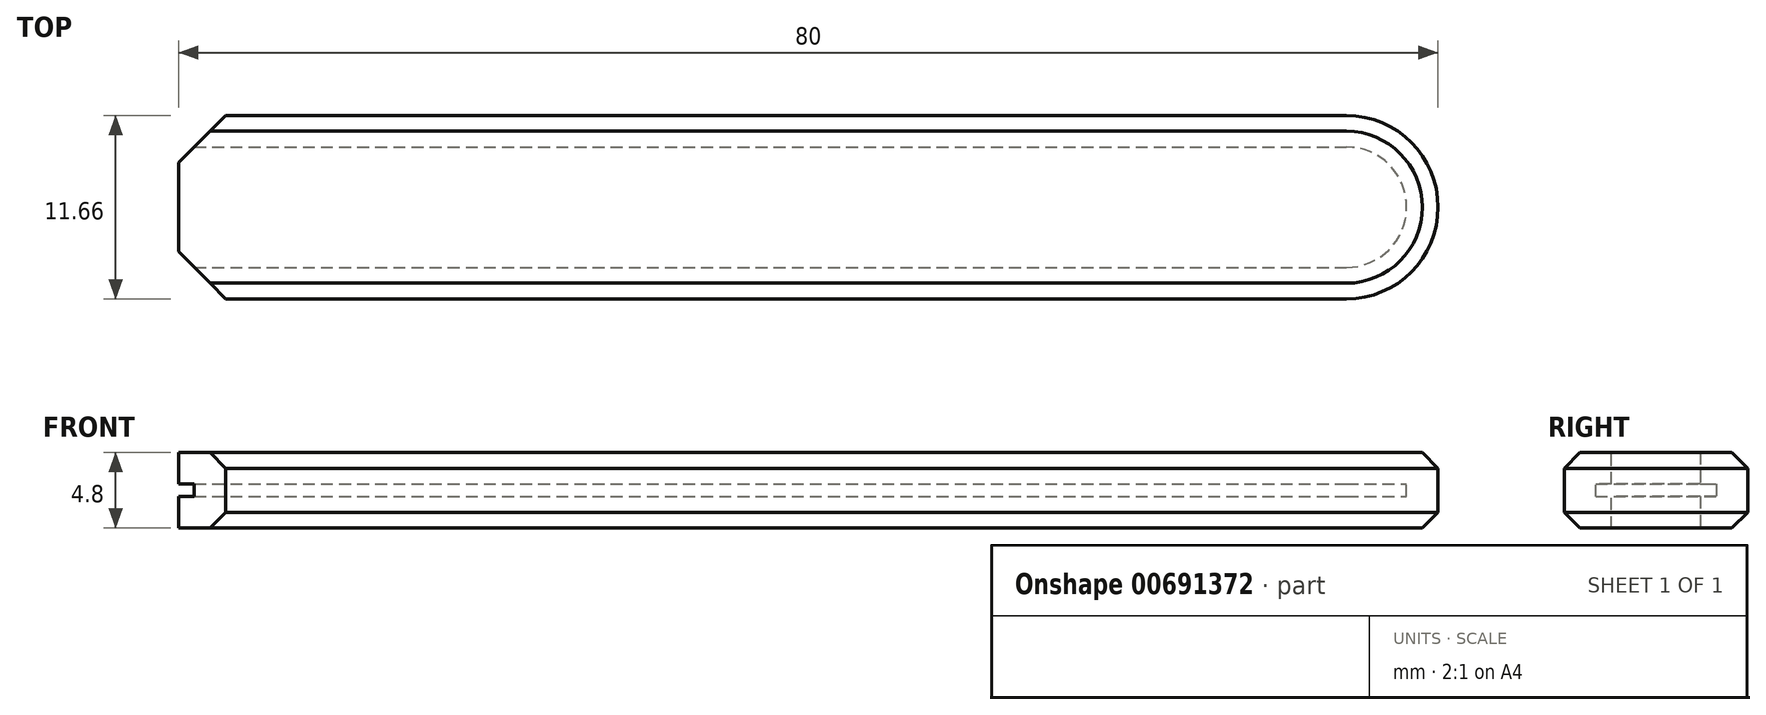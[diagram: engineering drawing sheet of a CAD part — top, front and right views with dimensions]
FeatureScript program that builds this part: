
annotation { "Feature Type Name" : "Feature", "Feature Type Description" : "" }
export const myFeature = defineFeature(function(context is Context, id is Id, definition is map)
    precondition{}
    {
        {
            var Q0;
            Q0=qCreatedBy(makeId("Top.planeOp"),FACE);
            var sketch = newSketch(context, id + "F0", { "sketchPlane" : qUnion([Q0])});
            skLineSegment(sketch, "E0.bottom", {"start": v(-39, -3.83) * mm, "end": v(35.17, -3.83) * mm});
            skLineSegment(sketch, "E0.top", {"start": v(-39, 3.82) * mm, "end": v(35.17, 3.82) * mm});
            skLineSegment(sketch, "E0.left", {"start": v(-39, -3.83) * mm, "end": v(-39, 3.82) * mm});
            skLineSegment(sketch, "E0.right", {"start": v(39, 0) * mm, "end": v(39, 0) * mm});
            skPoint(sketch, "E0.middle", {"position": v(0, 0) * mm});
            skPoint(sketch, "E1.visualSharp", {"position": v(39, 3.82) * mm});
            skArc(sketch, "E1.filletArc", {"start": v(39, 0) * mm, "mid": v(37.88, 2.7) * mm, "end": v(35.17, 3.82) * mm});
            skPoint(sketch, "E2.visualSharp", {"position": v(39, -3.83) * mm});
            skArc(sketch, "E2.filletArc", {"start": v(35.17, -3.83) * mm, "mid": v(37.88, -2.7) * mm, "end": v(39, 0) * mm});
            skLineSegment(sketch, "E3.0", {"start": v(-39, -5.83) * mm, "end": v(35.17, -5.83) * mm});
            skArc(sketch, "E3.1", {"start": v(35.17, -5.82) * mm, "mid": v(39.3, -4.12) * mm, "end": v(41, 0) * mm});
            skArc(sketch, "E3.2", {"start": v(41, 0) * mm, "mid": v(39.3, 4.12) * mm, "end": v(35.17, 5.82) * mm});
            skLineSegment(sketch, "E3.3", {"start": v(-39, 5.82) * mm, "end": v(35.17, 5.82) * mm});
            skLineSegment(sketch, "E4", {"start": v(-39, 5.82) * mm, "end": v(-39, 3.82) * mm});
            skLineSegment(sketch, "E5", {"start": v(-39, -5.83) * mm, "end": v(-39, -3.83) * mm});
            skSolve(sketch);
        }
        {
            var Q0;
            Q0=makeQuery(id+"F0.imprint","IMPRINT",FACE,{"disambiguationData":[TD([[makeQuery(id+"F0.imprint","IMPRINT",EDGE,{"derivedFrom":sQuery(id+"F0.wireOp",EDGE,"E0.bottom")}),-1.0]])]});
            var Q1;
            Q1=makeQuery(id+"F0.imprint","IMPRINT",FACE,{"disambiguationData":[TD([[makeQuery(id+"F0.imprint","IMPRINT",EDGE,{"derivedFrom":sQuery(id+"F0.wireOp",EDGE,"E0.bottom")}),1.0]])]});
            extrude(context, id + "F1", {"entities" : qUnion([Q0, Q1]), "depth" : 2 * mm, "offsetDistance" : 25 * mm});
        }
        {
            var Q0;
            Q0=makeQuery(id+"F0.imprint","IMPRINT",FACE,{"disambiguationData":[TD([[makeQuery(id+"F0.imprint","IMPRINT",EDGE,{"derivedFrom":sQuery(id+"F0.wireOp",EDGE,"E0.bottom")}),-1.0]])]});
            extrude(context, id + "F2", {"entities" : qUnion([Q0]), "operationType" : NewBodyOperationType.ADD, "oppositeDirection" : true, "depth" : .8 * mm, "offsetDistance" : 25 * mm});
        }
        {
            var Q0;
            Q0=makeQuery(id+"F2.opExtrude","CAP_FACE",FACE,{"disambiguationData":[OSD([sQuery(id+"F0.wireOp",EDGE,"E0.bottom"),sQuery(id+"F0.wireOp",EDGE,"E0.top"),sQuery(id+"F0.wireOp",EDGE,"E1.filletArc"),sQuery(id+"F0.wireOp",EDGE,"E2.filletArc"),sQuery(id+"F0.wireOp",EDGE,"E3.0"),sQuery(id+"F0.wireOp",EDGE,"E3.1"),sQuery(id+"F0.wireOp",EDGE,"E3.2"),sQuery(id+"F0.wireOp",EDGE,"E3.3"),sQuery(id+"F0.wireOp",EDGE,"E4"),sQuery(id+"F0.wireOp",EDGE,"E5")])],"isStart":false});
            var sketch = newSketch(context, id + "F3", { "sketchPlane" : qUnion([Q0])});
            skLineSegment(sketch, "E6", {"start": v(-39, -3.82) * mm, "end": v(-39, 3.83) * mm});
            skSolve(sketch);
        }
        {
            var Q0;
            Q0=makeQuery(id+"F3.imprint","IMPRINT",FACE,{"disambiguationData":[TD([[makeQuery(id+"F3.imprint","IMPRINT",EDGE,{"derivedFrom":sQuery(id+"F3.wireOp",EDGE,"E6")}),-1.0]])]});
            var Q1;
            Q1=makeQuery(id+"F3.imprint","IMPRINT",FACE,{"disambiguationData":[TD([[makeQuery(id+"F3.imprint","IMPRINT",EDGE,{"derivedFrom":makeQuery(id+"F2.opExtrude","CAP_EDGE",EDGE,{"disambiguationData":[OSD([sQuery(id+"F0.wireOp",EDGE,"E0.bottom")])],"isStart":false})}),1.0]])]});
            extrude(context, id + "F4", {"entities" : qUnion([Q0, Q1]), "operationType" : NewBodyOperationType.ADD, "depth" : 2 * mm, "offsetDistance" : 25 * mm});
        }
        {
            var Q0;
            Q0=makeQuery(id+"F4.opExtrude","CAP_EDGE",EDGE,{"disambiguationData":[OSD([sQuery(id+"F0.wireOp",EDGE,"E3.0")])],"isStart":false});
            var Q1;
            Q1=makeQuery(id+"F1.opExtrude","CAP_EDGE",EDGE,{"disambiguationData":[OSD([sQuery(id+"F0.wireOp",EDGE,"E3.0")])],"isStart":false});
            chamfer(context, id + "F5", {"entities" : qUnion([Q0, Q1]), "width" : 1 * mm, "tangentPropagation" : true});
        }
        {
            var Q0;
            {var subQ0=sQuery(id+"F0.wireOp",EDGE,"E5");var subQ1=sQuery(id+"F0.wireOp",EDGE,"E3.0");Q0=makeQuery(id+"F4.boolean.opBoolean","MERGE",EDGE,{"derivedFrom":[makeQuery(id+"F2.boolean.opBoolean","MERGE",EDGE,{"derivedFrom":[makeQuery(id+"F1.opExtrude","SWEPT_EDGE",EDGE,{"disambiguationData":[OSD([subQ1,subQ0])]}),makeQuery(id+"F2.opExtrude","SWEPT_EDGE",EDGE,{"disambiguationData":[OSD([subQ1,subQ0])]})]}),makeQuery(id+"F4.opExtrude","SWEPT_EDGE",EDGE,{"disambiguationData":[OSD([subQ1,subQ0])]})]});}
            var Q1;
            {var subQ0=sQuery(id+"F0.wireOp",EDGE,"E4");var subQ1=sQuery(id+"F0.wireOp",EDGE,"E3.3");Q1=makeQuery(id+"F4.boolean.opBoolean","MERGE",EDGE,{"derivedFrom":[makeQuery(id+"F2.boolean.opBoolean","MERGE",EDGE,{"derivedFrom":[makeQuery(id+"F1.opExtrude","SWEPT_EDGE",EDGE,{"disambiguationData":[OSD([subQ1,subQ0])]}),makeQuery(id+"F2.opExtrude","SWEPT_EDGE",EDGE,{"disambiguationData":[OSD([subQ1,subQ0])]})]}),makeQuery(id+"F4.opExtrude","SWEPT_EDGE",EDGE,{"disambiguationData":[OSD([subQ1,subQ0])]})]});}
            chamfer(context, id + "F6", {"entities" : qUnion([Q0, Q1]), "width" : 3 * mm, "tangentPropagation" : true});
        }
    });
